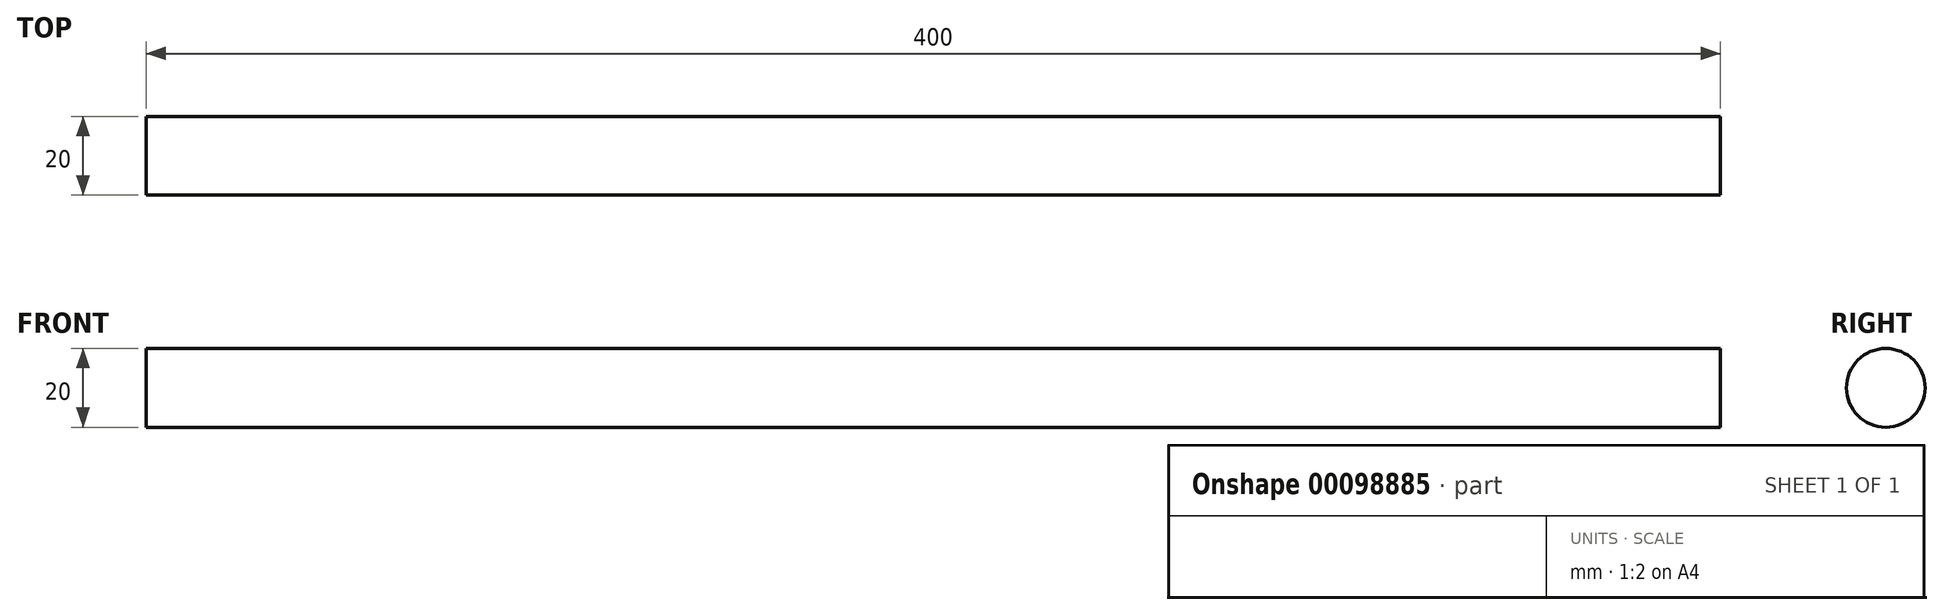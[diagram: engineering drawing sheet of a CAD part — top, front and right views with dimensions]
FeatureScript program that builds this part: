
annotation { "Feature Type Name" : "Feature", "Feature Type Description" : "" }
export const myFeature = defineFeature(function(context is Context, id is Id, definition is map)
    precondition{}
    {
        {
            var Q0;
            Q0=qCreatedBy(makeId("Right.planeOp"),FACE);
            var sketch = newSketch(context, id + "F0", { "sketchPlane" : qUnion([Q0])});
            skCircle(sketch, "E0", {"center": v(0, 0) * mm, "radius": 10 * mm});
            skSolve(sketch);
        }
        {
            var Q0;
            Q0 = qSketchRegion(id + "F0", true);
            extrude(context, id + "F1", {"entities" : qUnion([Q0]), "endBound" : BoundingType.SYMMETRIC, "depth" : 400 * mm});
        }
    });
